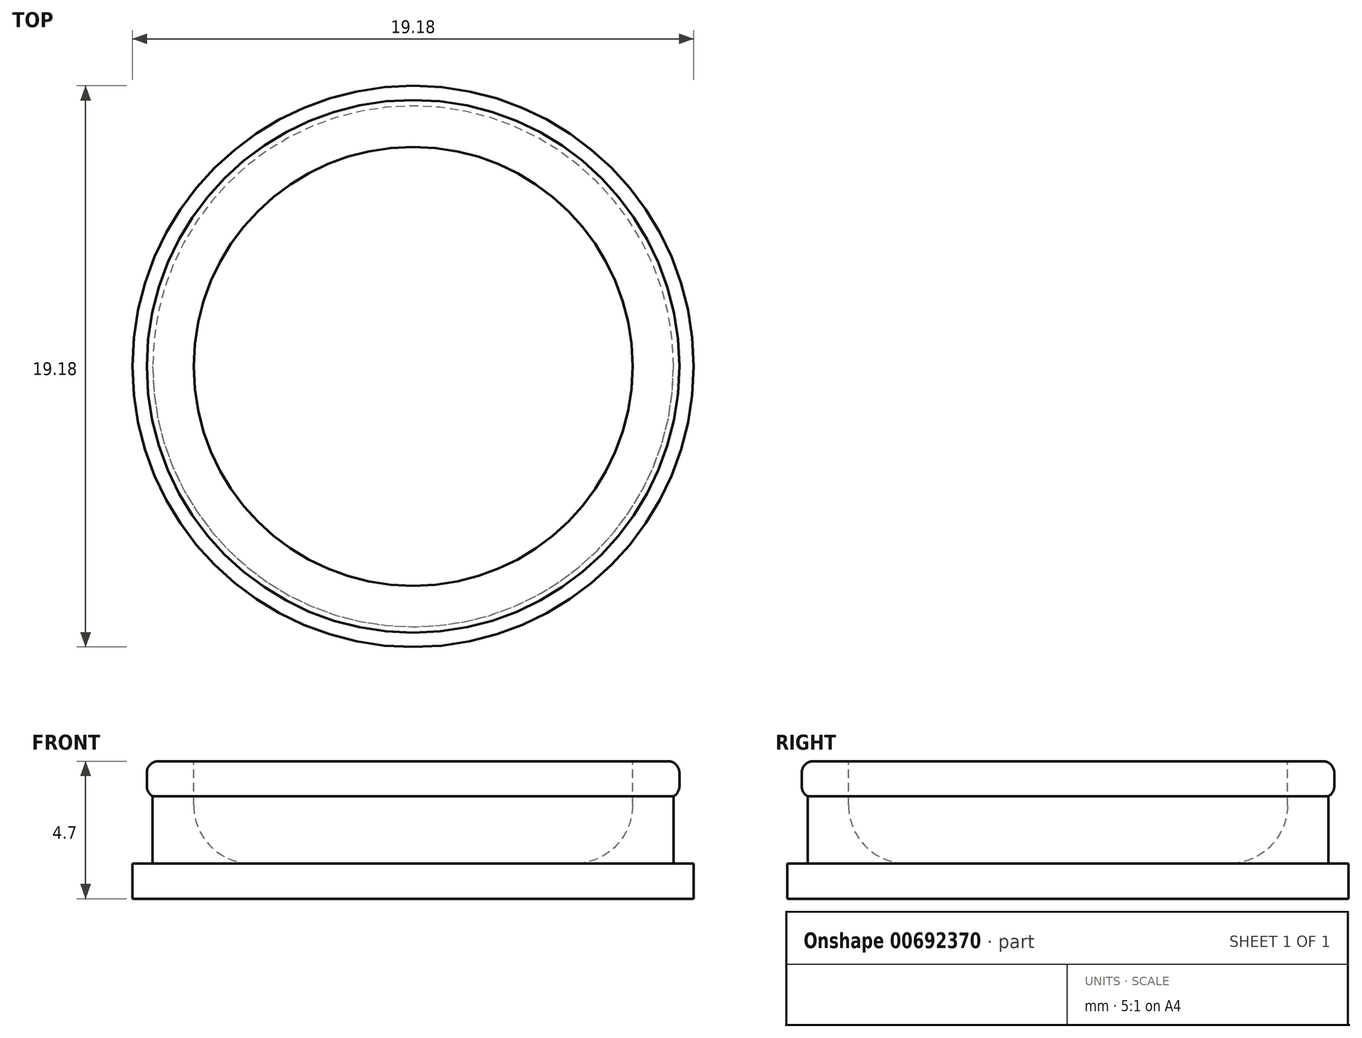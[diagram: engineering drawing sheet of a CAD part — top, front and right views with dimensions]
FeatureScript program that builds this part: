
annotation { "Feature Type Name" : "Feature", "Feature Type Description" : "" }
export const myFeature = defineFeature(function(context is Context, id is Id, definition is map)
    precondition{}
    {
        {
            var Q0;
            Q0=qCreatedBy(makeId("Front.planeOp"),FACE);
            var sketch = newSketch(context, id + "F0", { "sketchPlane" : qUnion([Q0])});
            skLineSegment(sketch, "E0", {"start": v(0, 0) * mm, "end": v(-9.6, 0) * mm});
            skLineSegment(sketch, "E1", {"start": v(-9.6, 0) * mm, "end": v(-9.6, 1.2) * mm});
            skLineSegment(sketch, "E2", {"start": v(-9.6, 1.2) * mm, "end": v(-8.9, 1.2) * mm});
            skLineSegment(sketch, "E3", {"start": v(-8.9, 1.2) * mm, "end": v(-8.9, 3.5) * mm});
            skLineSegment(sketch, "E4", {"start": v(-8.9, 3.5) * mm, "end": v(-9.1, 3.5) * mm});
            skLineSegment(sketch, "E5", {"start": v(-9.1, 3.5) * mm, "end": v(-9.1, 4.7) * mm});
            skLineSegment(sketch, "E6", {"start": v(-9.1, 4.7) * mm, "end": v(-7.5, 4.7) * mm});
            skLineSegment(sketch, "E7", {"start": v(-7.5, 4.7) * mm, "end": v(-7.5, 1.2) * mm});
            skLineSegment(sketch, "E8", {"start": v(-7.5, 1.2) * mm, "end": v(0, 1.2) * mm});
            skLineSegment(sketch, "E9", {"start": v(0, 1.2) * mm, "end": v(0, 0) * mm});
            skSolve(sketch);
        }
        {
            var Q0;
            Q0 = qSketchRegion(id + "F0", true);
            var Q1;
            Q1=sQuery(id+"F0.wireOp",EDGE,"E9");
            revolve(context, id + "F1", {"entities" : qUnion([Q0]), "axis" : qUnion([Q1]), "revolveType" : RevolveType.FULL});
        }
        {
            var Q0;
            Q0=makeQuery(id+"F1.opRevolve","SWEPT_EDGE",EDGE,{"disambiguationData":[OSD([sQuery(id+"F0.wireOp",EDGE,"E7"),sQuery(id+"F0.wireOp",EDGE,"E8")])]});
            fillet(context, id + "F2", {"entities" : qUnion([Q0]), "radius" : 2 * mm, "tangentPropagation" : true, "allowEdgeOverflow" : false});
        }
        {
            var Q0;
            Q0=makeQuery(id+"F1.opRevolve","SWEPT_EDGE",EDGE,{"disambiguationData":[OSD([sQuery(id+"F0.wireOp",EDGE,"E5"),sQuery(id+"F0.wireOp",EDGE,"E6")])]});
            var Q1;
            Q1=makeQuery(id+"F1.opRevolve","SWEPT_EDGE",EDGE,{"disambiguationData":[OSD([sQuery(id+"F0.wireOp",EDGE,"E4"),sQuery(id+"F0.wireOp",EDGE,"E5")])]});
            fillet(context, id + "F3", {"entities" : qUnion([Q0, Q1]), "radius" : 0.4 * mm, "tangentPropagation" : true, "allowEdgeOverflow" : false});
        }
    });
